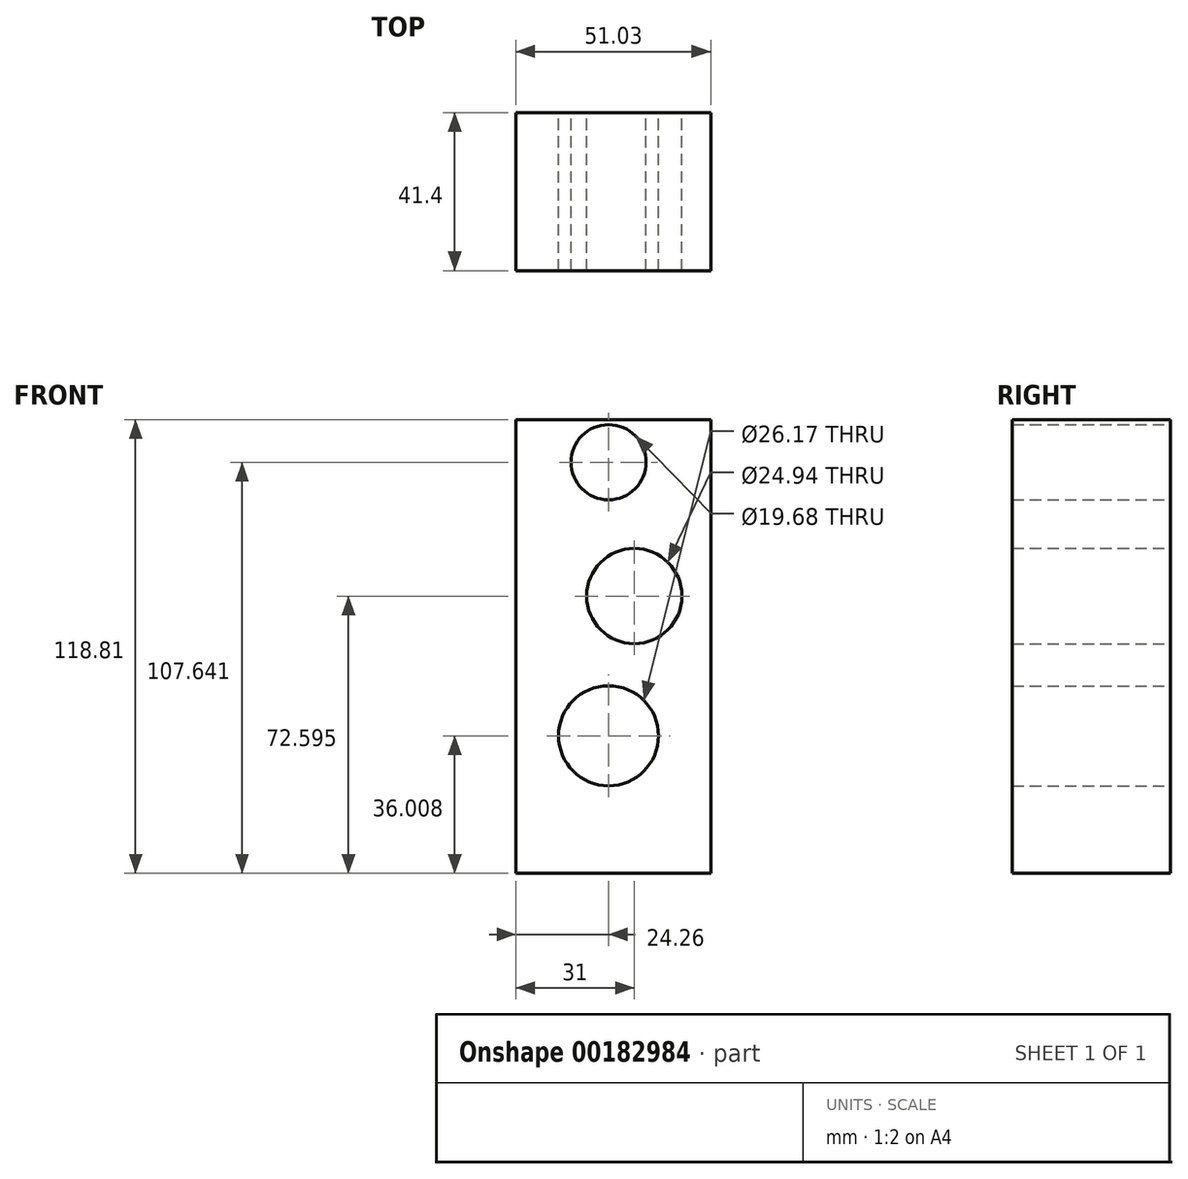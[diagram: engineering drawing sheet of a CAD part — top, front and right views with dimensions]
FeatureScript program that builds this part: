
annotation { "Feature Type Name" : "Feature", "Feature Type Description" : "" }
export const myFeature = defineFeature(function(context is Context, id is Id, definition is map)
    precondition{}
    {
        {
            var Q0;
            Q0=qCreatedBy(makeId("Front.planeOp"),FACE);
            var sketch = newSketch(context, id + "F0", { "sketchPlane" : qUnion([Q0])});
            skLineSegment(sketch, "E0.bottom", {"start": v(26.77, 56.7) * mm, "end": v(-24.26, 56.7) * mm});
            skLineSegment(sketch, "E0.top", {"start": v(26.77, -62.1) * mm, "end": v(-24.26, -62.1) * mm});
            skLineSegment(sketch, "E0.left", {"start": v(26.77, 56.7) * mm, "end": v(26.77, -62.1) * mm});
            skLineSegment(sketch, "E0.right", {"start": v(-24.26, 56.7) * mm, "end": v(-24.26, -62.1) * mm});
            skCircle(sketch, "E1", {"center": v(6.74, 10.5) * mm, "radius": 12.47 * mm});
            skCircle(sketch, "E2", {"center": v(0, -26.1) * mm, "radius": 13.09 * mm});
            skCircle(sketch, "E3", {"center": v(0, 45.54) * mm, "radius": 9.84 * mm});
            skSolve(sketch);
        }
        {
            var Q0;
            Q0 = qSketchRegion(id + "F0", true);
            extrude(context, id + "F1", {"entities" : qUnion([Q0]), "depth" : 41.4 * mm});
        }
        {
            var Q0;
            Q0 = qSketchRegion(id + "F0", true);
            extrude(context, id + "F2", {"entities" : qUnion([Q0]), "operationType" : NewBodyOperationType.ADD, "depth" : 25.4 * mm});
        }
    });
